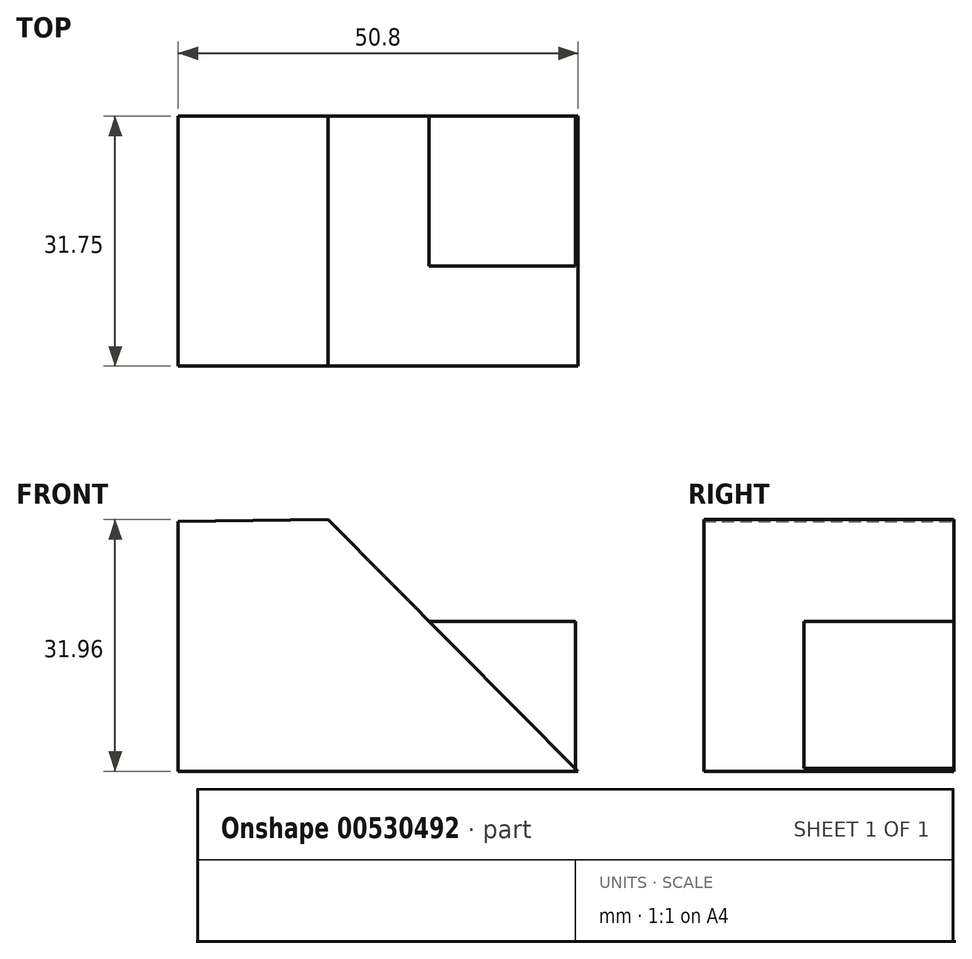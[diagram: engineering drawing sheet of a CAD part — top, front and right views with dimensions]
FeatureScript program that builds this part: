
annotation { "Feature Type Name" : "Feature", "Feature Type Description" : "" }
export const myFeature = defineFeature(function(context is Context, id is Id, definition is map)
    precondition{}
    {
        {
            var Q0;
            Q0=qCreatedBy(makeId("Front.planeOp"),FACE);
            var sketch = newSketch(context, id + "F0", { "sketchPlane" : qUnion([Q0])});
            skLineSegment(sketch, "E0", {"start": v(-57.52, 31.75) * mm, "end": v(-57.52, 0) * mm});
            skLineSegment(sketch, "E1", {"start": v(-57.52, 0) * mm, "end": v(-6.72, 0) * mm});
            skLineSegment(sketch, "E2", {"start": v(-6.72, 0) * mm, "end": v(-38.47, 31.96) * mm});
            skLineSegment(sketch, "E3", {"start": v(-38.47, 31.96) * mm, "end": v(-57.52, 31.75) * mm});
            skSolve(sketch);
        }
        {
            var Q0;
            Q0 = qSketchRegion(id + "F0", true);
            extrude(context, id + "F1", {"entities" : qUnion([Q0]), "depth" : 31.75 * mm, "offsetDistance" : 25.4 * mm});
        }
        {
            var Q0;
            Q0=qCreatedBy(makeId("Front.planeOp"),FACE);
            var sketch = newSketch(context, id + "F2", { "sketchPlane" : qUnion([Q0])});
            skLineSegment(sketch, "E4", {"start": v(-26.1, 19.05) * mm, "end": v(-7.05, 19.05) * mm});
            skLineSegment(sketch, "E5", {"start": v(-7.05, 19.05) * mm, "end": v(-7.05, 0) * mm});
            skLineSegment(sketch, "E6", {"start": v(-26.1, 19.05) * mm, "end": v(-7.05, 0) * mm});
            skSolve(sketch);
        }
        {
            var Q0;
            Q0 = qSketchRegion(id + "F2", true);
            extrude(context, id + "F3", {"entities" : qUnion([Q0]), "operationType" : NewBodyOperationType.ADD, "depth" : 19.05 * mm, "offsetDistance" : 25.4 * mm});
        }
    });
